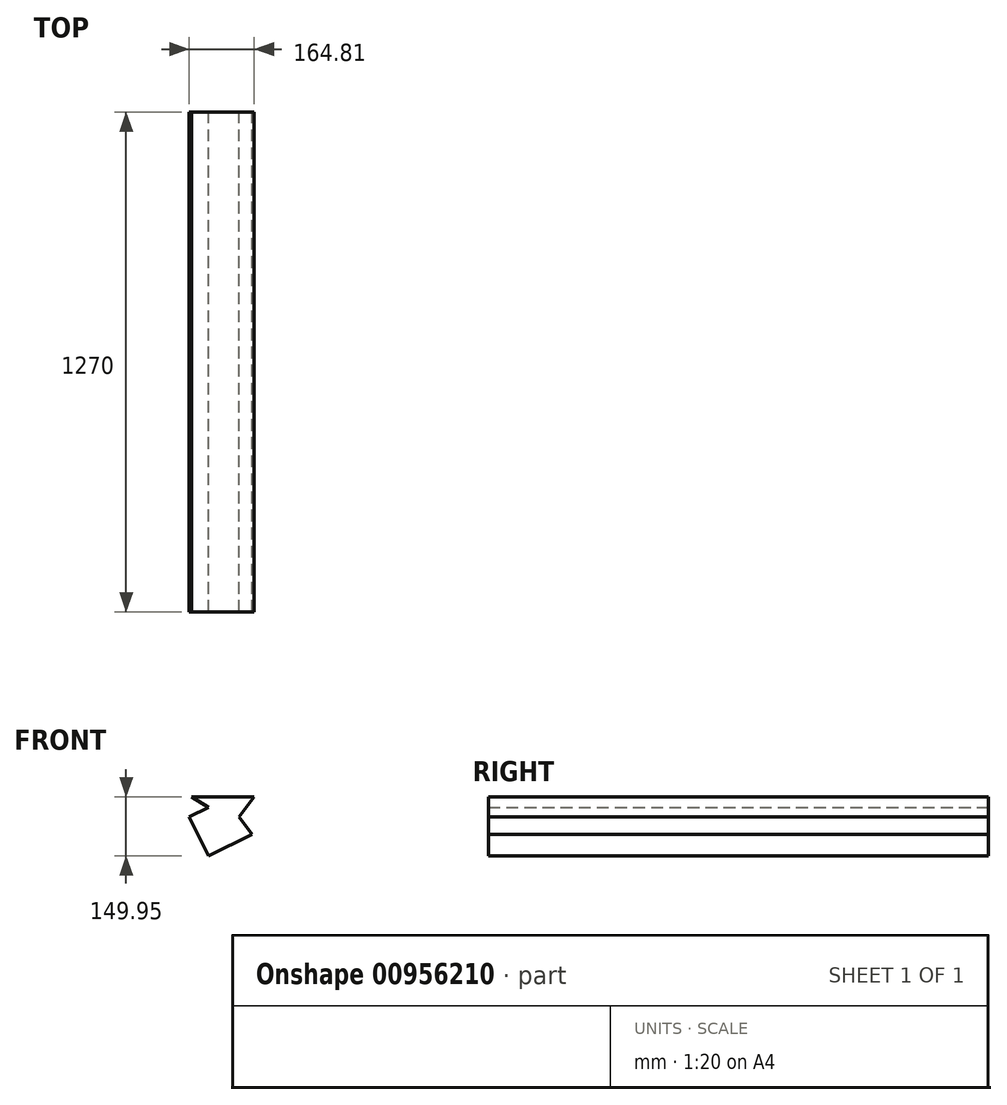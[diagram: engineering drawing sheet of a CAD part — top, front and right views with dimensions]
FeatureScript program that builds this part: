
annotation { "Feature Type Name" : "Feature", "Feature Type Description" : "" }
export const myFeature = defineFeature(function(context is Context, id is Id, definition is map)
    precondition{}
    {
        {
            var Q0;
            Q0=qCreatedBy(makeId("Front.planeOp"),FACE);
            var sketch = newSketch(context, id + "F0", { "sketchPlane" : qUnion([Q0])});
            skLineSegment(sketch, "E0", {"start": v(-76.54, 71.1) * mm, "end": v(82.4, 71.1) * mm});
            skLineSegment(sketch, "E1", {"start": v(82.4, 71.1) * mm, "end": v(44.23, 19.9) * mm});
            skLineSegment(sketch, "E2", {"start": v(44.23, 19.9) * mm, "end": v(77, -24.09) * mm});
            skLineSegment(sketch, "E3", {"start": v(77, -24.09) * mm, "end": v(-33.44, -78.86) * mm});
            skLineSegment(sketch, "E4", {"start": v(-33.44, -78.86) * mm, "end": v(-82.42, 19.9) * mm});
            skLineSegment(sketch, "E5", {"start": v(-82.42, 19.9) * mm, "end": v(-33.44, 44.2) * mm});
            skLineSegment(sketch, "E6", {"start": v(-33.44, 44.2) * mm, "end": v(-76.54, 71.1) * mm});
            skSolve(sketch);
        }
        {
            var Q0;
            Q0 = qSketchRegion(id + "F0", true);
            extrude(context, id + "F1", {"entities" : qUnion([Q0]), "depth" : 1270 * mm, "offsetDistance" : 25.4 * mm});
        }
    });
